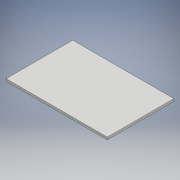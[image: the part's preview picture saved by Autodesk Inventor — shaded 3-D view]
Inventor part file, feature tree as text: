
AUTODESK INVENTOR PART (.ipt)
format: ipt  version: 2018.2 (Build 222227000, 227)  size: 94,720 bytes
history: native  units: mm
features: sketch x2, extrude x1
ambient origin geometry x8: Origin, YZ Plane, XZ Plane, XY Plane, X Axis, Y Axis, Z Axis, Center Point
bodies: Solid1 (feature_tree)
feature tree (3):
  sketch  "Sketch1"  dims[d0=85.0mm d1=56.0mm]
  extrude  "Extrusion1"  Depth=56.0mm
  sketch  "Sketch2"  dims[d2=2.0mm d3=0.0mm]
